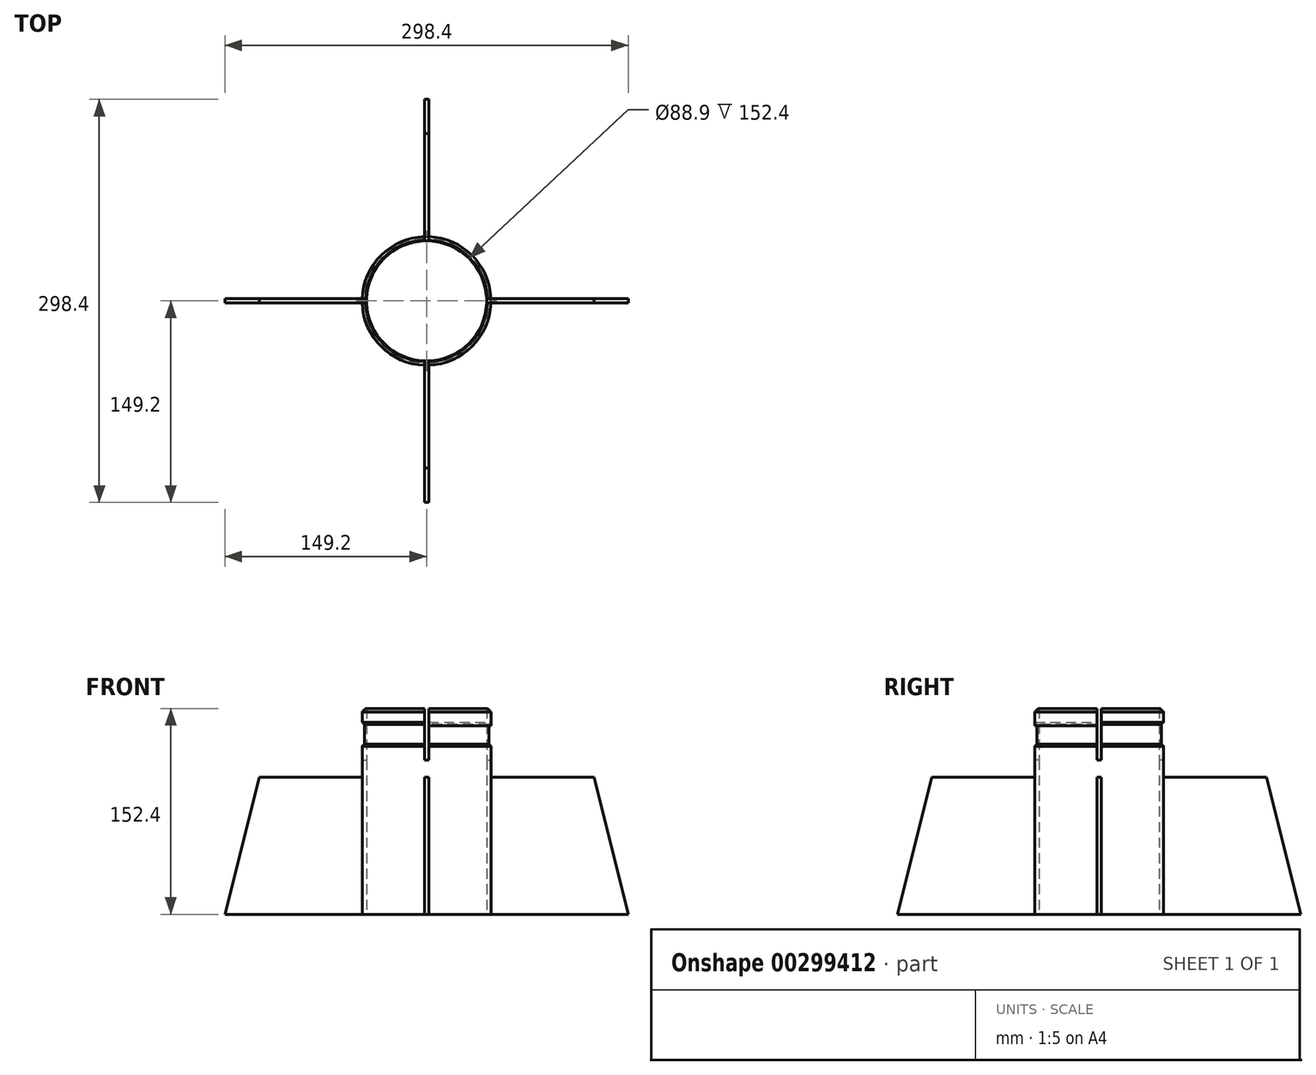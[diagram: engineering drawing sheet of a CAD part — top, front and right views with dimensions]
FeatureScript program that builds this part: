
annotation { "Feature Type Name" : "Feature", "Feature Type Description" : "" }
export const myFeature = defineFeature(function(context is Context, id is Id, definition is map)
    precondition{}
    {
        {
            var Q0;
            Q0=qCreatedBy(makeId("Top.planeOp"),FACE);
            var sketch = newSketch(context, id + "F0", { "sketchPlane" : qUnion([Q0])});
            skCircle(sketch, "E0", {"center": v(0, 0) * mm, "radius": 44.45 * mm});
            skArc(sketch, "E1.0", {"start": v(47.6, 1.59) * mm, "mid": v(33.68, 33.68) * mm, "end": v(1.59, 47.6) * mm});
            skLineSegment(sketch, "E2.0", {"start": v(-1.59, 104.78) * mm, "end": v(-1.59, 104.76) * mm});
            skLineSegment(sketch, "E3.0", {"start": v(-101.6, -1.59) * mm, "end": v(-47.6, -1.59) * mm});
            skLineSegment(sketch, "E4.MirrorCS", {"start": v(-101.6, 1.59) * mm, "end": v(-47.6, 1.59) * mm});
            skLineSegment(sketch, "E5.MirrorCS", {"start": v(1.59, 104.78) * mm, "end": v(1.59, 104.76) * mm});
            skLineSegment(sketch, "E6.trimOffspring", {"start": v(1.59, -47.6) * mm, "end": v(1.59, -101.6) * mm});
            skLineSegment(sketch, "E7.trimOffspring", {"start": v(-1.59, -47.6) * mm, "end": v(-1.59, -101.6) * mm});
            skLineSegment(sketch, "E8.trimOffspring", {"start": v(47.6, -1.59) * mm, "end": v(101.6, -1.59) * mm});
            skLineSegment(sketch, "E9.trimOffspring", {"start": v(47.6, 1.59) * mm, "end": v(101.6, 1.59) * mm});
            skArc(sketch, "E10.trimOffspring", {"start": v(-1.59, 47.6) * mm, "mid": v(-33.68, 33.68) * mm, "end": v(-47.6, 1.59) * mm});
            skArc(sketch, "E11.trimOffspring", {"start": v(-47.6, -1.59) * mm, "mid": v(-33.68, -33.68) * mm, "end": v(-1.59, -47.6) * mm});
            skArc(sketch, "E12.trimOffspring", {"start": v(1.59, -47.6) * mm, "mid": v(33.68, -33.68) * mm, "end": v(47.6, -1.59) * mm});
            skLineSegment(sketch, "E13.trimOffspring", {"start": v(-1.59, 101.59) * mm, "end": v(-1.59, 47.6) * mm});
            skLineSegment(sketch, "E14.trimOffspring", {"start": v(1.59, 101.59) * mm, "end": v(1.59, 47.6) * mm});
            skLineSegment(sketch, "E15", {"start": v(-101.6, 1.59) * mm, "end": v(-101.6, -1.59) * mm});
            skLineSegment(sketch, "E16", {"start": v(-1.59, 101.59) * mm, "end": v(1.59, 101.59) * mm});
            skLineSegment(sketch, "E17", {"start": v(101.6, 1.59) * mm, "end": v(101.6, -1.59) * mm});
            skLineSegment(sketch, "E18", {"start": v(1.59, -101.6) * mm, "end": v(-1.59, -101.6) * mm});
            skSolve(sketch);
        }
        {
            var Q0;
            Q0 = qSketchRegion(id + "F0", true);
            extrude(context, id + "F1", {"entities" : qUnion([Q0]), "depth" : 76.2 * mm});
        }
        {
            var Q0;
            Q0=qCreatedBy(makeId("Top.planeOp"),FACE);
            var sketch = newSketch(context, id + "F2", { "sketchPlane" : qUnion([Q0])});
            skCircle(sketch, "E19", {"center": v(0, 0) * mm, "radius": 47.63 * mm});
            skCircle(sketch, "E20.0", {"center": v(0, 0) * mm, "radius": 44.45 * mm});
            skSolve(sketch);
        }
        {
            var Q0;
            Q0 = qSketchRegion(id + "F2", true);
            extrude(context, id + "F3", {"entities" : qUnion([Q0]), "operationType" : NewBodyOperationType.ADD, "depth" : 127 * mm});
        }
        {
            var Q0;
            Q0=makeQuery(id+"F3.opExtrude","CAP_FACE",FACE,{"disambiguationData":[OSD([sQuery(id+"F2.wireOp",EDGE,"E19"),sQuery(id+"F2.wireOp",EDGE,"E20.0")])],"isStart":false});
            var sketch = newSketch(context, id + "F4", { "sketchPlane" : qUnion([Q0])});
            skLineSegment(sketch, "E21.0", {"start": v(-1.59, 47.62) * mm, "end": v(-1.59, -47.62) * mm});
            skLineSegment(sketch, "E22.MirrorCS", {"start": v(1.59, 47.62) * mm, "end": v(1.59, -47.62) * mm});
            skLineSegment(sketch, "E23.0", {"start": v(-47.62, -1.59) * mm, "end": v(47.62, -1.59) * mm});
            skLineSegment(sketch, "E24.MirrorCS", {"start": v(-47.62, 1.59) * mm, "end": v(47.62, 1.59) * mm});
            skLineSegment(sketch, "E25", {"start": v(-47.62, -1.59) * mm, "end": v(-47.62, 1.59) * mm});
            skLineSegment(sketch, "E26", {"start": v(-1.59, 47.62) * mm, "end": v(1.59, 47.62) * mm});
            skLineSegment(sketch, "E27", {"start": v(47.62, 1.59) * mm, "end": v(47.62, -1.59) * mm});
            skLineSegment(sketch, "E28", {"start": v(1.59, -47.62) * mm, "end": v(-1.59, -47.62) * mm});
            skPoint(sketch, "E29.orphan", {"position": v(-47.62, 47.62) * mm});
            skPoint(sketch, "E30.orphan", {"position": v(-47.62, -47.62) * mm});
            skPoint(sketch, "E31.orphan", {"position": v(47.62, -47.62) * mm});
            skPoint(sketch, "E32.orphan", {"position": v(47.62, 47.62) * mm});
            skSolve(sketch);
        }
        {
            var Q0;
            Q0 = qSketchRegion(id + "F4", true);
            extrude(context, id + "F5", {"entities" : qUnion([Q0]), "operationType" : NewBodyOperationType.REMOVE, "oppositeDirection" : true, "depth" : 38.1 * mm});
        }
        {
            var Q0;
            Q0=qCreatedBy(makeId("Right.planeOp"),FACE);
            var sketch = newSketch(context, id + "F6", { "sketchPlane" : qUnion([Q0])});
            skLineSegment(sketch, "E33", {"start": v(0, 0) * mm, "end": v(0, 127) * mm});
            skLineSegment(sketch, "E34", {"start": v(0, 127) * mm, "end": v(-47.63, 127) * mm});
            skLineSegment(sketch, "E35", {"start": v(-47.63, 127) * mm, "end": v(-47.63, 114.3) * mm});
            skLineSegment(sketch, "E36", {"start": v(-47.63, 114.3) * mm, "end": v(-46.04, 114.3) * mm});
            skLineSegment(sketch, "E37", {"start": v(-46.04, 114.3) * mm, "end": v(-46.04, 101.6) * mm});
            skLineSegment(sketch, "E38", {"start": v(-46.04, 101.6) * mm, "end": v(-47.63, 101.6) * mm});
            skLineSegment(sketch, "E39", {"start": v(-47.63, 101.6) * mm, "end": v(-47.63, 114.3) * mm});
            skSolve(sketch);
        }
        {
            var Q0;
            Q0 = qSketchRegion(id + "F6", true);
            var Q1;
            Q1=sQuery(id+"F6.wireOp",EDGE,"E33");
            revolve(context, id + "F7", {"operationType" : NewBodyOperationType.REMOVE, "entities" : qUnion([Q0]), "axis" : qUnion([Q1]), "revolveType" : RevolveType.FULL, "oppositeDirection" : true});
        }
        {
            var Q0;
            {var subQ0=sQuery(id+"F2.wireOp",EDGE,"E19");var subQ1=sQuery(id+"F4.wireOp",EDGE,"E23.0");var subQ2=sQuery(id+"F4.wireOp",EDGE,"E21.0");var subQ3=makeQuery(id+"F4.imprint","INTERSECT",VERTEX,{"derivedFrom":[subQ2,subQ1]});var subQ7=makeQuery(id+"F3.opExtrude","CAP_EDGE",EDGE,{"disambiguationData":[OSD([subQ0])],"isStart":false});var subQ9=makeQuery(id+"F4.imprint","INTERSECT",VERTEX,{"disambiguationData":[OD(1.0)],"derivedFrom":[subQ7,subQ2]});Q0=makeQuery(id+"F5.boolean.opBoolean","SPLIT",EDGE,{"disambiguationData":[TD([makeQuery(id+"F5.opExtrude","SWEPT_FACE",FACE,{"disambiguationData":[OSD([subQ2]),TDD([makeQuery(id+"F4.imprint","IMPRINT",EDGE,{"disambiguationData":[TD([[subQ3,-1.0]])],"derivedFrom":subQ2}),makeQuery(id+"F4.imprint","IMPRINT",EDGE,{"disambiguationData":[TD([[subQ9,1.0]])],"derivedFrom":subQ2}),makeQuery(id+"F4.imprint","IMPRINT",EDGE,{"disambiguationData":[TD([[makeQuery(id+"F4.imprint","INTERSECT",VERTEX,{"derivedFrom":[subQ2,sQuery(id+"F4.wireOp",EDGE,"E28")]}),1.0]])],"derivedFrom":subQ2})])]})])],"derivedFrom":subQ7});}
            var Q1;
            {var subQ0=sQuery(id+"F2.wireOp",EDGE,"E19");var subQ1=sQuery(id+"F4.wireOp",EDGE,"E23.0");var subQ2=sQuery(id+"F4.wireOp",EDGE,"E21.0");var subQ3=makeQuery(id+"F4.imprint","INTERSECT",VERTEX,{"derivedFrom":[subQ2,subQ1]});var subQ6=makeQuery(id+"F3.opExtrude","CAP_EDGE",EDGE,{"disambiguationData":[OSD([subQ0])],"isStart":false});var subQ8=makeQuery(id+"F4.imprint","INTERSECT",VERTEX,{"disambiguationData":[OD(1.0)],"derivedFrom":[subQ6,subQ2]});var subQ10=sQuery(id+"F6.wireOp",EDGE,"E36");Q1=makeQuery(id+"F7.boolean.opBoolean","COPY",EDGE,{"disambiguationData":[TD([makeQuery(id+"F5.boolean.opBoolean","COPY",FACE,{"derivedFrom":makeQuery(id+"F5.opExtrude","SWEPT_FACE",FACE,{"disambiguationData":[OSD([subQ2]),TDD([makeQuery(id+"F4.imprint","IMPRINT",EDGE,{"disambiguationData":[TD([[subQ3,-1.0]])],"derivedFrom":subQ2}),makeQuery(id+"F4.imprint","IMPRINT",EDGE,{"disambiguationData":[TD([[subQ8,1.0]])],"derivedFrom":subQ2}),makeQuery(id+"F4.imprint","IMPRINT",EDGE,{"disambiguationData":[TD([[makeQuery(id+"F4.imprint","INTERSECT",VERTEX,{"derivedFrom":[subQ2,sQuery(id+"F4.wireOp",EDGE,"E28")]}),1.0]])],"derivedFrom":subQ2})])]})})])],"derivedFrom":makeQuery(id+"F7.opRevolve","SWEPT_EDGE",EDGE,{"disambiguationData":[OSD([subQ10,sQuery(id+"F6.wireOp",EDGE,"E39")])]})});}
            var Q2;
            {var subQ0=sQuery(id+"F6.wireOp",EDGE,"E38");var subQ1=sQuery(id+"F2.wireOp",EDGE,"E19");var subQ2=sQuery(id+"F4.wireOp",EDGE,"E23.0");var subQ3=sQuery(id+"F4.wireOp",EDGE,"E21.0");var subQ4=makeQuery(id+"F4.imprint","INTERSECT",VERTEX,{"derivedFrom":[subQ3,subQ2]});var subQ7=makeQuery(id+"F3.opExtrude","CAP_EDGE",EDGE,{"disambiguationData":[OSD([subQ1])],"isStart":false});var subQ9=makeQuery(id+"F4.imprint","INTERSECT",VERTEX,{"disambiguationData":[OD(1.0)],"derivedFrom":[subQ7,subQ3]});Q2=makeQuery(id+"F7.boolean.opBoolean","COPY",EDGE,{"disambiguationData":[TD([makeQuery(id+"F5.boolean.opBoolean","COPY",FACE,{"derivedFrom":makeQuery(id+"F5.opExtrude","SWEPT_FACE",FACE,{"disambiguationData":[OSD([subQ3]),TDD([makeQuery(id+"F4.imprint","IMPRINT",EDGE,{"disambiguationData":[TD([[subQ4,-1.0]])],"derivedFrom":subQ3}),makeQuery(id+"F4.imprint","IMPRINT",EDGE,{"disambiguationData":[TD([[subQ9,1.0]])],"derivedFrom":subQ3}),makeQuery(id+"F4.imprint","IMPRINT",EDGE,{"disambiguationData":[TD([[makeQuery(id+"F4.imprint","INTERSECT",VERTEX,{"derivedFrom":[subQ3,sQuery(id+"F4.wireOp",EDGE,"E28")]}),1.0]])],"derivedFrom":subQ3})])]})})])],"derivedFrom":makeQuery(id+"F7.opRevolve","SWEPT_EDGE",EDGE,{"disambiguationData":[OSD([subQ0,sQuery(id+"F6.wireOp",EDGE,"E39")])]})});}
            var Q3;
            {var subQ0=sQuery(id+"F4.wireOp",EDGE,"E22.MirrorCS");var subQ1=sQuery(id+"F2.wireOp",EDGE,"E19");var subQ2=makeQuery(id+"F3.opExtrude","CAP_EDGE",EDGE,{"disambiguationData":[OSD([subQ1])],"isStart":false});var subQ3=makeQuery(id+"F4.imprint","INTERSECT",VERTEX,{"disambiguationData":[OD(1.0)],"derivedFrom":[subQ2,subQ0]});var subQ6=sQuery(id+"F4.wireOp",EDGE,"E23.0");var subQ7=makeQuery(id+"F4.imprint","INTERSECT",VERTEX,{"derivedFrom":[subQ0,subQ6]});var subQ8=sQuery(id+"F6.wireOp",EDGE,"E38");Q3=makeQuery(id+"F7.boolean.opBoolean","COPY",EDGE,{"disambiguationData":[TD([makeQuery(id+"F5.boolean.opBoolean","COPY",FACE,{"derivedFrom":makeQuery(id+"F5.opExtrude","SWEPT_FACE",FACE,{"disambiguationData":[OSD([subQ0]),TDD([makeQuery(id+"F4.imprint","IMPRINT",EDGE,{"disambiguationData":[TD([[subQ7,-1.0]])],"derivedFrom":subQ0}),makeQuery(id+"F4.imprint","IMPRINT",EDGE,{"disambiguationData":[TD([[subQ3,1.0]])],"derivedFrom":subQ0}),makeQuery(id+"F4.imprint","IMPRINT",EDGE,{"disambiguationData":[TD([[makeQuery(id+"F4.imprint","INTERSECT",VERTEX,{"derivedFrom":[subQ0,sQuery(id+"F4.wireOp",EDGE,"E28")]}),1.0]])],"derivedFrom":subQ0})])]})})])],"derivedFrom":makeQuery(id+"F7.opRevolve","SWEPT_EDGE",EDGE,{"disambiguationData":[OSD([subQ8,sQuery(id+"F6.wireOp",EDGE,"E39")])]})});}
            var Q4;
            {var subQ0=sQuery(id+"F4.wireOp",EDGE,"E22.MirrorCS");var subQ1=sQuery(id+"F2.wireOp",EDGE,"E19");var subQ2=makeQuery(id+"F3.opExtrude","CAP_EDGE",EDGE,{"disambiguationData":[OSD([subQ1])],"isStart":false});var subQ3=makeQuery(id+"F4.imprint","INTERSECT",VERTEX,{"disambiguationData":[OD(1.0)],"derivedFrom":[subQ2,subQ0]});var subQ6=sQuery(id+"F4.wireOp",EDGE,"E23.0");var subQ7=makeQuery(id+"F4.imprint","INTERSECT",VERTEX,{"derivedFrom":[subQ0,subQ6]});var subQ10=sQuery(id+"F6.wireOp",EDGE,"E36");Q4=makeQuery(id+"F7.boolean.opBoolean","COPY",EDGE,{"disambiguationData":[TD([makeQuery(id+"F5.boolean.opBoolean","COPY",FACE,{"derivedFrom":makeQuery(id+"F5.opExtrude","SWEPT_FACE",FACE,{"disambiguationData":[OSD([subQ0]),TDD([makeQuery(id+"F4.imprint","IMPRINT",EDGE,{"disambiguationData":[TD([[subQ7,-1.0]])],"derivedFrom":subQ0}),makeQuery(id+"F4.imprint","IMPRINT",EDGE,{"disambiguationData":[TD([[subQ3,1.0]])],"derivedFrom":subQ0}),makeQuery(id+"F4.imprint","IMPRINT",EDGE,{"disambiguationData":[TD([[makeQuery(id+"F4.imprint","INTERSECT",VERTEX,{"derivedFrom":[subQ0,sQuery(id+"F4.wireOp",EDGE,"E28")]}),1.0]])],"derivedFrom":subQ0})])]})})])],"derivedFrom":makeQuery(id+"F7.opRevolve","SWEPT_EDGE",EDGE,{"disambiguationData":[OSD([subQ10,sQuery(id+"F6.wireOp",EDGE,"E39")])]})});}
            var Q5;
            {var subQ0=sQuery(id+"F4.wireOp",EDGE,"E23.0");var subQ1=sQuery(id+"F2.wireOp",EDGE,"E19");var subQ2=makeQuery(id+"F3.opExtrude","CAP_EDGE",EDGE,{"disambiguationData":[OSD([subQ1])],"isStart":false});var subQ7=sQuery(id+"F4.wireOp",EDGE,"E22.MirrorCS");var subQ8=makeQuery(id+"F4.imprint","INTERSECT",VERTEX,{"derivedFrom":[subQ7,subQ0]});var subQ9=makeQuery(id+"F4.imprint","INTERSECT",VERTEX,{"disambiguationData":[OD(1.0)],"derivedFrom":[subQ2,subQ7]});Q5=makeQuery(id+"F5.boolean.opBoolean","SPLIT",EDGE,{"disambiguationData":[TD([makeQuery(id+"F5.opExtrude","SWEPT_FACE",FACE,{"disambiguationData":[OSD([subQ7]),TDD([makeQuery(id+"F4.imprint","IMPRINT",EDGE,{"disambiguationData":[TD([[subQ8,-1.0]])],"derivedFrom":subQ7}),makeQuery(id+"F4.imprint","IMPRINT",EDGE,{"disambiguationData":[TD([[subQ9,1.0]])],"derivedFrom":subQ7}),makeQuery(id+"F4.imprint","IMPRINT",EDGE,{"disambiguationData":[TD([[makeQuery(id+"F4.imprint","INTERSECT",VERTEX,{"derivedFrom":[subQ7,sQuery(id+"F4.wireOp",EDGE,"E28")]}),1.0]])],"derivedFrom":subQ7})])]})])],"derivedFrom":subQ2});}
            var Q6;
            {var subQ0=sQuery(id+"F2.wireOp",EDGE,"E19");var subQ1=sQuery(id+"F4.wireOp",EDGE,"E24.MirrorCS");var subQ2=sQuery(id+"F4.wireOp",EDGE,"E21.0");var subQ3=makeQuery(id+"F4.imprint","INTERSECT",VERTEX,{"derivedFrom":[subQ2,subQ1]});var subQ6=makeQuery(id+"F3.opExtrude","CAP_EDGE",EDGE,{"disambiguationData":[OSD([subQ0])],"isStart":false});var subQ7=makeQuery(id+"F4.imprint","INTERSECT",VERTEX,{"disambiguationData":[OD(0.0)],"derivedFrom":[subQ6,subQ2]});var subQ10=sQuery(id+"F6.wireOp",EDGE,"E36");Q6=makeQuery(id+"F7.boolean.opBoolean","COPY",EDGE,{"disambiguationData":[TD([makeQuery(id+"F5.boolean.opBoolean","COPY",FACE,{"derivedFrom":makeQuery(id+"F5.opExtrude","SWEPT_FACE",FACE,{"disambiguationData":[OSD([subQ2]),TDD([makeQuery(id+"F4.imprint","IMPRINT",EDGE,{"disambiguationData":[TD([[makeQuery(id+"F4.imprint","INTERSECT",VERTEX,{"derivedFrom":[subQ2,sQuery(id+"F4.wireOp",EDGE,"E26")]}),-1.0]])],"derivedFrom":subQ2}),makeQuery(id+"F4.imprint","IMPRINT",EDGE,{"disambiguationData":[TD([[subQ7,-1.0]])],"derivedFrom":subQ2}),makeQuery(id+"F4.imprint","IMPRINT",EDGE,{"disambiguationData":[TD([[subQ3,1.0]])],"derivedFrom":subQ2})])]})})])],"derivedFrom":makeQuery(id+"F7.opRevolve","SWEPT_EDGE",EDGE,{"disambiguationData":[OSD([subQ10,sQuery(id+"F6.wireOp",EDGE,"E39")])]})});}
            var Q7;
            {var subQ0=sQuery(id+"F2.wireOp",EDGE,"E19");var subQ2=sQuery(id+"F4.wireOp",EDGE,"E24.MirrorCS");var subQ3=sQuery(id+"F4.wireOp",EDGE,"E21.0");var subQ4=makeQuery(id+"F4.imprint","INTERSECT",VERTEX,{"derivedFrom":[subQ3,subQ2]});var subQ7=makeQuery(id+"F3.opExtrude","CAP_EDGE",EDGE,{"disambiguationData":[OSD([subQ0])],"isStart":false});var subQ10=makeQuery(id+"F4.imprint","INTERSECT",VERTEX,{"disambiguationData":[OD(0.0)],"derivedFrom":[subQ7,subQ3]});Q7=makeQuery(id+"F5.boolean.opBoolean","SPLIT",EDGE,{"disambiguationData":[TD([makeQuery(id+"F5.opExtrude","SWEPT_FACE",FACE,{"disambiguationData":[OSD([subQ3]),TDD([makeQuery(id+"F4.imprint","IMPRINT",EDGE,{"disambiguationData":[TD([[makeQuery(id+"F4.imprint","INTERSECT",VERTEX,{"derivedFrom":[subQ3,sQuery(id+"F4.wireOp",EDGE,"E26")]}),-1.0]])],"derivedFrom":subQ3}),makeQuery(id+"F4.imprint","IMPRINT",EDGE,{"disambiguationData":[TD([[subQ10,-1.0]])],"derivedFrom":subQ3}),makeQuery(id+"F4.imprint","IMPRINT",EDGE,{"disambiguationData":[TD([[subQ4,1.0]])],"derivedFrom":subQ3})])]})])],"derivedFrom":subQ7});}
            var Q8;
            {var subQ0=sQuery(id+"F6.wireOp",EDGE,"E38");var subQ1=sQuery(id+"F2.wireOp",EDGE,"E19");var subQ2=sQuery(id+"F4.wireOp",EDGE,"E24.MirrorCS");var subQ3=sQuery(id+"F4.wireOp",EDGE,"E21.0");var subQ4=makeQuery(id+"F4.imprint","INTERSECT",VERTEX,{"derivedFrom":[subQ3,subQ2]});var subQ7=makeQuery(id+"F3.opExtrude","CAP_EDGE",EDGE,{"disambiguationData":[OSD([subQ1])],"isStart":false});var subQ8=makeQuery(id+"F4.imprint","INTERSECT",VERTEX,{"disambiguationData":[OD(0.0)],"derivedFrom":[subQ7,subQ3]});Q8=makeQuery(id+"F7.boolean.opBoolean","COPY",EDGE,{"disambiguationData":[TD([makeQuery(id+"F5.boolean.opBoolean","COPY",FACE,{"derivedFrom":makeQuery(id+"F5.opExtrude","SWEPT_FACE",FACE,{"disambiguationData":[OSD([subQ3]),TDD([makeQuery(id+"F4.imprint","IMPRINT",EDGE,{"disambiguationData":[TD([[makeQuery(id+"F4.imprint","INTERSECT",VERTEX,{"derivedFrom":[subQ3,sQuery(id+"F4.wireOp",EDGE,"E26")]}),-1.0]])],"derivedFrom":subQ3}),makeQuery(id+"F4.imprint","IMPRINT",EDGE,{"disambiguationData":[TD([[subQ8,-1.0]])],"derivedFrom":subQ3}),makeQuery(id+"F4.imprint","IMPRINT",EDGE,{"disambiguationData":[TD([[subQ4,1.0]])],"derivedFrom":subQ3})])]})})])],"derivedFrom":makeQuery(id+"F7.opRevolve","SWEPT_EDGE",EDGE,{"disambiguationData":[OSD([subQ0,sQuery(id+"F6.wireOp",EDGE,"E39")])]})});}
            var Q9;
            {var subQ0=sQuery(id+"F2.wireOp",EDGE,"E19");var subQ2=sQuery(id+"F4.wireOp",EDGE,"E24.MirrorCS");var subQ3=makeQuery(id+"F3.opExtrude","CAP_EDGE",EDGE,{"disambiguationData":[OSD([subQ0])],"isStart":false});var subQ7=sQuery(id+"F4.wireOp",EDGE,"E22.MirrorCS");var subQ8=makeQuery(id+"F4.imprint","INTERSECT",VERTEX,{"derivedFrom":[subQ7,subQ2]});var subQ10=makeQuery(id+"F4.imprint","INTERSECT",VERTEX,{"disambiguationData":[OD(0.0)],"derivedFrom":[subQ3,subQ7]});Q9=makeQuery(id+"F5.boolean.opBoolean","SPLIT",EDGE,{"disambiguationData":[TD([makeQuery(id+"F5.opExtrude","SWEPT_FACE",FACE,{"disambiguationData":[OSD([subQ7]),TDD([makeQuery(id+"F4.imprint","IMPRINT",EDGE,{"disambiguationData":[TD([[makeQuery(id+"F4.imprint","INTERSECT",VERTEX,{"derivedFrom":[subQ7,sQuery(id+"F4.wireOp",EDGE,"E26")]}),-1.0]])],"derivedFrom":subQ7}),makeQuery(id+"F4.imprint","IMPRINT",EDGE,{"disambiguationData":[TD([[subQ10,-1.0]])],"derivedFrom":subQ7}),makeQuery(id+"F4.imprint","IMPRINT",EDGE,{"disambiguationData":[TD([[subQ8,1.0]])],"derivedFrom":subQ7})])]})])],"derivedFrom":subQ3});}
            var Q10;
            {var subQ0=sQuery(id+"F2.wireOp",EDGE,"E19");var subQ1=sQuery(id+"F4.wireOp",EDGE,"E24.MirrorCS");var subQ2=sQuery(id+"F4.wireOp",EDGE,"E22.MirrorCS");var subQ3=makeQuery(id+"F4.imprint","INTERSECT",VERTEX,{"derivedFrom":[subQ2,subQ1]});var subQ6=makeQuery(id+"F3.opExtrude","CAP_EDGE",EDGE,{"disambiguationData":[OSD([subQ0])],"isStart":false});var subQ7=makeQuery(id+"F4.imprint","INTERSECT",VERTEX,{"disambiguationData":[OD(0.0)],"derivedFrom":[subQ6,subQ2]});var subQ10=sQuery(id+"F6.wireOp",EDGE,"E36");Q10=makeQuery(id+"F7.boolean.opBoolean","COPY",EDGE,{"disambiguationData":[TD([makeQuery(id+"F5.boolean.opBoolean","COPY",FACE,{"derivedFrom":makeQuery(id+"F5.opExtrude","SWEPT_FACE",FACE,{"disambiguationData":[OSD([subQ2]),TDD([makeQuery(id+"F4.imprint","IMPRINT",EDGE,{"disambiguationData":[TD([[makeQuery(id+"F4.imprint","INTERSECT",VERTEX,{"derivedFrom":[subQ2,sQuery(id+"F4.wireOp",EDGE,"E26")]}),-1.0]])],"derivedFrom":subQ2}),makeQuery(id+"F4.imprint","IMPRINT",EDGE,{"disambiguationData":[TD([[subQ7,-1.0]])],"derivedFrom":subQ2}),makeQuery(id+"F4.imprint","IMPRINT",EDGE,{"disambiguationData":[TD([[subQ3,1.0]])],"derivedFrom":subQ2})])]})})])],"derivedFrom":makeQuery(id+"F7.opRevolve","SWEPT_EDGE",EDGE,{"disambiguationData":[OSD([subQ10,sQuery(id+"F6.wireOp",EDGE,"E39")])]})});}
            var Q11;
            {var subQ0=sQuery(id+"F6.wireOp",EDGE,"E38");var subQ1=sQuery(id+"F2.wireOp",EDGE,"E19");var subQ2=sQuery(id+"F4.wireOp",EDGE,"E24.MirrorCS");var subQ3=sQuery(id+"F4.wireOp",EDGE,"E22.MirrorCS");var subQ4=makeQuery(id+"F4.imprint","INTERSECT",VERTEX,{"derivedFrom":[subQ3,subQ2]});var subQ7=makeQuery(id+"F3.opExtrude","CAP_EDGE",EDGE,{"disambiguationData":[OSD([subQ1])],"isStart":false});var subQ8=makeQuery(id+"F4.imprint","INTERSECT",VERTEX,{"disambiguationData":[OD(0.0)],"derivedFrom":[subQ7,subQ3]});Q11=makeQuery(id+"F7.boolean.opBoolean","COPY",EDGE,{"disambiguationData":[TD([makeQuery(id+"F5.boolean.opBoolean","COPY",FACE,{"derivedFrom":makeQuery(id+"F5.opExtrude","SWEPT_FACE",FACE,{"disambiguationData":[OSD([subQ3]),TDD([makeQuery(id+"F4.imprint","IMPRINT",EDGE,{"disambiguationData":[TD([[makeQuery(id+"F4.imprint","INTERSECT",VERTEX,{"derivedFrom":[subQ3,sQuery(id+"F4.wireOp",EDGE,"E26")]}),-1.0]])],"derivedFrom":subQ3}),makeQuery(id+"F4.imprint","IMPRINT",EDGE,{"disambiguationData":[TD([[subQ8,-1.0]])],"derivedFrom":subQ3}),makeQuery(id+"F4.imprint","IMPRINT",EDGE,{"disambiguationData":[TD([[subQ4,1.0]])],"derivedFrom":subQ3})])]})})])],"derivedFrom":makeQuery(id+"F7.opRevolve","SWEPT_EDGE",EDGE,{"disambiguationData":[OSD([subQ0,sQuery(id+"F6.wireOp",EDGE,"E39")])]})});}
            chamfer(context, id + "F8", {"entities" : qUnion([Q0, Q1, Q2, Q3, Q4, Q5, Q6, Q7, Q8, Q9, Q10, Q11]), "width" : 2.54 * mm, "tangentPropagation" : true});
        }
        {
            var Q0;
            Q0=makeQuery(id+"F1.opExtrude","CAP_FACE",FACE,{"disambiguationData":[OSD([sQuery(id+"F0.wireOp",EDGE,"E0"),sQuery(id+"F0.wireOp",EDGE,"E1.0"),sQuery(id+"F0.wireOp",EDGE,"E3.0"),sQuery(id+"F0.wireOp",EDGE,"E4.MirrorCS"),sQuery(id+"F0.wireOp",EDGE,"E6.trimOffspring"),sQuery(id+"F0.wireOp",EDGE,"E7.trimOffspring"),sQuery(id+"F0.wireOp",EDGE,"E8.trimOffspring"),sQuery(id+"F0.wireOp",EDGE,"E9.trimOffspring"),sQuery(id+"F0.wireOp",EDGE,"E10.trimOffspring"),sQuery(id+"F0.wireOp",EDGE,"E11.trimOffspring"),sQuery(id+"F0.wireOp",EDGE,"E12.trimOffspring"),sQuery(id+"F0.wireOp",EDGE,"E13.trimOffspring"),sQuery(id+"F0.wireOp",EDGE,"E14.trimOffspring"),sQuery(id+"F0.wireOp",EDGE,"E15"),sQuery(id+"F0.wireOp",EDGE,"E16"),sQuery(id+"F0.wireOp",EDGE,"E17"),sQuery(id+"F0.wireOp",EDGE,"E18")])],"isStart":true});
            extrude(context, id + "F9", {"entities" : qUnion([Q0]), "operationType" : NewBodyOperationType.ADD, "depth" : 25.4 * mm});
        }
        {
            var Q0;
            {var subQ0=sQuery(id+"F0.wireOp",EDGE,"E4.MirrorCS");Q0=makeQuery(id+"F9.boolean.opBoolean","MERGE",FACE,{"derivedFrom":[makeQuery(id+"F1.opExtrude","SWEPT_FACE",FACE,{"disambiguationData":[OSD([subQ0])]}),makeQuery(id+"F9.opExtrude","SWEPT_FACE",FACE,{"disambiguationData":[OSD([subQ0])]})]});}
            var sketch = newSketch(context, id + "F10", { "sketchPlane" : qUnion([Q0])});
            skLineSegment(sketch, "E40", {"start": v(47.6, 76.2) * mm, "end": v(123.8, 76.2) * mm});
            skLineSegment(sketch, "E41", {"start": v(47.6, -25.4) * mm, "end": v(149.2, -25.4) * mm});
            skLineSegment(sketch, "E42", {"start": v(149.2, -25.4) * mm, "end": v(123.8, 76.2) * mm});
            skLineSegment(sketch, "E43", {"start": v(101.6, 76.2) * mm, "end": v(101.6, -25.4) * mm});
            skSolve(sketch);
        }
        {
            var Q0;
            Q0 = qSketchRegion(id + "F10", true);
            var Q1;
            {var subQ0=sQuery(id+"F0.wireOp",EDGE,"E3.0");Q1=makeQuery(id+"F9.boolean.opBoolean","MERGE",FACE,{"derivedFrom":[makeQuery(id+"F1.opExtrude","SWEPT_FACE",FACE,{"disambiguationData":[OSD([subQ0])]}),makeQuery(id+"F9.opExtrude","SWEPT_FACE",FACE,{"disambiguationData":[OSD([subQ0])]})]});}
            extrude(context, id + "F11", {"entities" : qUnion([Q0]), "operationType" : NewBodyOperationType.ADD, "endBound" : BoundingType.UP_TO_SURFACE, "oppositeDirection" : true, "endBoundEntityFace" : qUnion([Q1]), "depth" : 25.4 * mm});
        }
        {
            var Q0;
            {var subQ0=sQuery(id+"F0.wireOp",EDGE,"E14.trimOffspring");Q0=makeQuery(id+"F9.boolean.opBoolean","MERGE",FACE,{"derivedFrom":[makeQuery(id+"F1.opExtrude","SWEPT_FACE",FACE,{"disambiguationData":[OSD([subQ0])]}),makeQuery(id+"F9.opExtrude","SWEPT_FACE",FACE,{"disambiguationData":[OSD([subQ0])]})]});}
            var sketch = newSketch(context, id + "F12", { "sketchPlane" : qUnion([Q0])});
            skLineSegment(sketch, "E44", {"start": v(47.6, -25.4) * mm, "end": v(149.2, -25.4) * mm});
            skLineSegment(sketch, "E45", {"start": v(47.6, 76.2) * mm, "end": v(123.8, 76.2) * mm});
            skLineSegment(sketch, "E46", {"start": v(123.8, 76.2) * mm, "end": v(149.2, -25.4) * mm});
            skLineSegment(sketch, "E47", {"start": v(101.59, -25.4) * mm, "end": v(101.59, 76.2) * mm});
            skSolve(sketch);
        }
        {
            var Q0;
            Q0 = qSketchRegion(id + "F12", true);
            var Q1;
            {var subQ0=sQuery(id+"F0.wireOp",EDGE,"E13.trimOffspring");Q1=makeQuery(id+"F9.boolean.opBoolean","MERGE",FACE,{"derivedFrom":[makeQuery(id+"F1.opExtrude","SWEPT_FACE",FACE,{"disambiguationData":[OSD([subQ0])]}),makeQuery(id+"F9.opExtrude","SWEPT_FACE",FACE,{"disambiguationData":[OSD([subQ0])]})]});}
            extrude(context, id + "F13", {"entities" : qUnion([Q0]), "operationType" : NewBodyOperationType.ADD, "endBound" : BoundingType.UP_TO_SURFACE, "oppositeDirection" : true, "endBoundEntityFace" : qUnion([Q1]), "depth" : 25.4 * mm});
        }
        {
            var Q0;
            {var subQ0=sQuery(id+"F0.wireOp",EDGE,"E8.trimOffspring");Q0=makeQuery(id+"F9.boolean.opBoolean","MERGE",FACE,{"derivedFrom":[makeQuery(id+"F1.opExtrude","SWEPT_FACE",FACE,{"disambiguationData":[OSD([subQ0])]}),makeQuery(id+"F9.opExtrude","SWEPT_FACE",FACE,{"disambiguationData":[OSD([subQ0])]})]});}
            var sketch = newSketch(context, id + "F14", { "sketchPlane" : qUnion([Q0])});
            skLineSegment(sketch, "E48", {"start": v(47.6, 76.2) * mm, "end": v(123.8, 76.2) * mm});
            skLineSegment(sketch, "E49", {"start": v(47.6, -25.4) * mm, "end": v(149.2, -25.4) * mm});
            skLineSegment(sketch, "E50", {"start": v(149.2, -25.4) * mm, "end": v(123.8, 76.2) * mm});
            skLineSegment(sketch, "E51", {"start": v(101.6, 76.2) * mm, "end": v(101.6, -25.4) * mm});
            skSolve(sketch);
        }
        {
            var Q0;
            Q0 = qSketchRegion(id + "F14", true);
            var Q1;
            {var subQ0=sQuery(id+"F0.wireOp",EDGE,"E9.trimOffspring");Q1=makeQuery(id+"F9.boolean.opBoolean","MERGE",FACE,{"derivedFrom":[makeQuery(id+"F1.opExtrude","SWEPT_FACE",FACE,{"disambiguationData":[OSD([subQ0])]}),makeQuery(id+"F9.opExtrude","SWEPT_FACE",FACE,{"disambiguationData":[OSD([subQ0])]})]});}
            extrude(context, id + "F15", {"entities" : qUnion([Q0]), "operationType" : NewBodyOperationType.ADD, "endBound" : BoundingType.UP_TO_SURFACE, "oppositeDirection" : true, "endBoundEntityFace" : qUnion([Q1]), "depth" : 25.4 * mm});
        }
        {
            var Q0;
            {var subQ0=sQuery(id+"F0.wireOp",EDGE,"E7.trimOffspring");Q0=makeQuery(id+"F9.boolean.opBoolean","MERGE",FACE,{"derivedFrom":[makeQuery(id+"F1.opExtrude","SWEPT_FACE",FACE,{"disambiguationData":[OSD([subQ0])]}),makeQuery(id+"F9.opExtrude","SWEPT_FACE",FACE,{"disambiguationData":[OSD([subQ0])]})]});}
            var sketch = newSketch(context, id + "F16", { "sketchPlane" : qUnion([Q0])});
            skLineSegment(sketch, "E52", {"start": v(47.6, 76.2) * mm, "end": v(123.8, 76.2) * mm});
            skLineSegment(sketch, "E53", {"start": v(47.6, -25.4) * mm, "end": v(149.2, -25.4) * mm});
            skLineSegment(sketch, "E54", {"start": v(149.2, -25.4) * mm, "end": v(123.8, 76.2) * mm});
            skLineSegment(sketch, "E55", {"start": v(101.6, 76.2) * mm, "end": v(101.6, -25.4) * mm});
            skSolve(sketch);
        }
        {
            var Q0;
            Q0 = qSketchRegion(id + "F16", true);
            var Q1;
            {var subQ0=sQuery(id+"F0.wireOp",EDGE,"E6.trimOffspring");Q1=makeQuery(id+"F9.boolean.opBoolean","MERGE",FACE,{"derivedFrom":[makeQuery(id+"F1.opExtrude","SWEPT_FACE",FACE,{"disambiguationData":[OSD([subQ0])]}),makeQuery(id+"F9.opExtrude","SWEPT_FACE",FACE,{"disambiguationData":[OSD([subQ0])]})]});}
            extrude(context, id + "F17", {"entities" : qUnion([Q0]), "operationType" : NewBodyOperationType.ADD, "endBound" : BoundingType.UP_TO_SURFACE, "oppositeDirection" : true, "endBoundEntityFace" : qUnion([Q1]), "depth" : 25.4 * mm});
        }
    });
